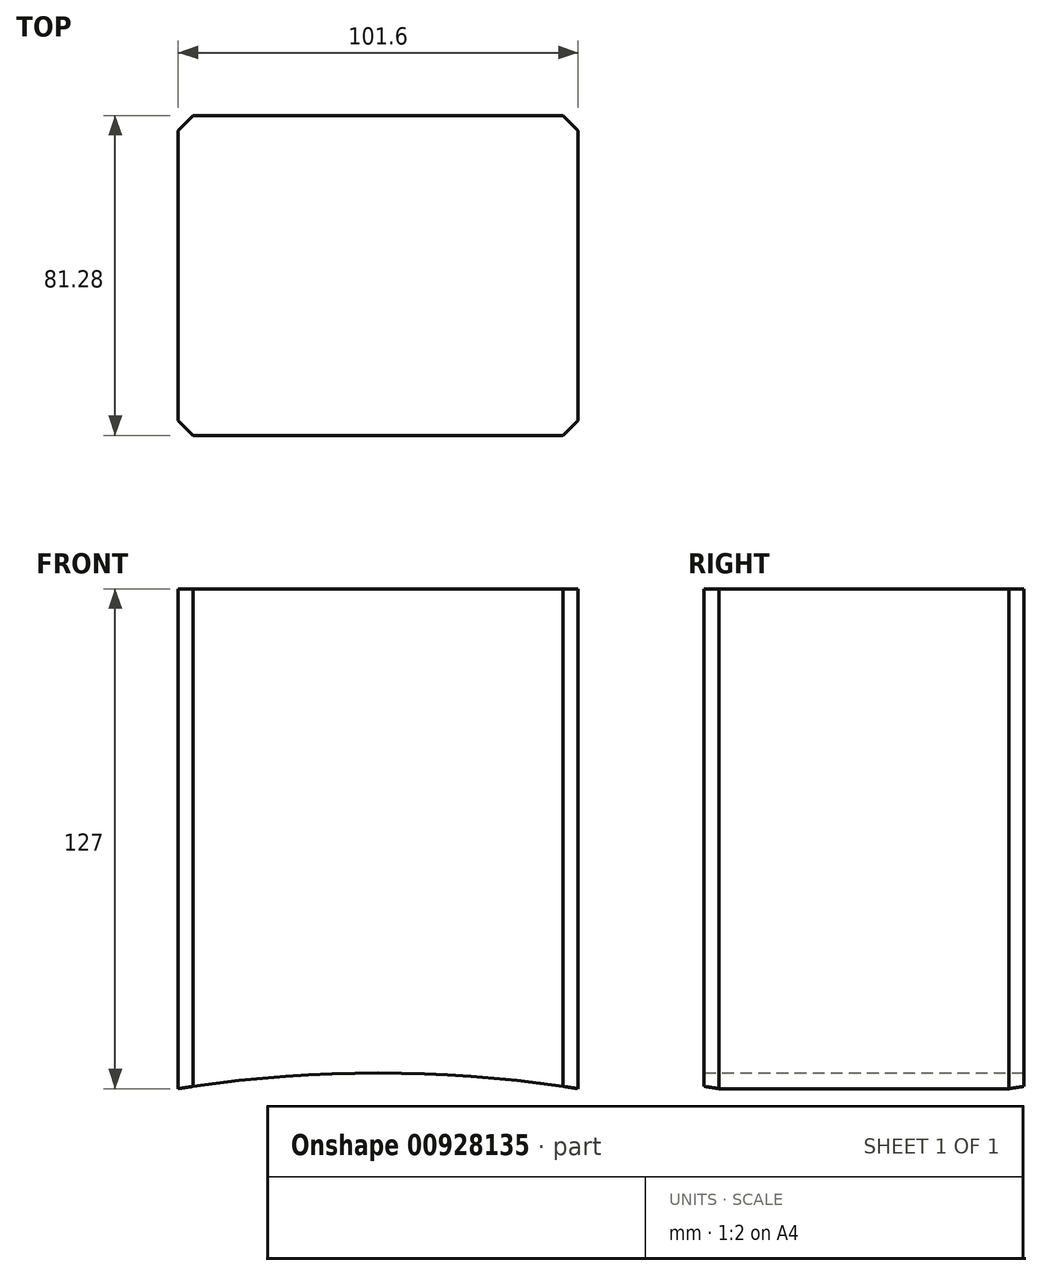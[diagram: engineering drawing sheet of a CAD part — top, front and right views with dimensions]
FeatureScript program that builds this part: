
annotation { "Feature Type Name" : "Feature", "Feature Type Description" : "" }
export const myFeature = defineFeature(function(context is Context, id is Id, definition is map)
    precondition{}
    {
        {
            var Q0;
            Q0=qCreatedBy(makeId("Front.planeOp"),FACE);
            var sketch = newSketch(context, id + "F0", { "sketchPlane" : qUnion([Q0])});
            skArc(sketch, "E0", {"start": v(58.46, 0) * mm, "mid": v(7.66, 4) * mm, "end": v(-43.14, 0) * mm});
            skLineSegment(sketch, "E1", {"start": v(58.46, 0) * mm, "end": v(58.46, 127) * mm});
            skLineSegment(sketch, "E2", {"start": v(58.46, 127) * mm, "end": v(-43.14, 127) * mm});
            skLineSegment(sketch, "E3", {"start": v(-43.14, 127) * mm, "end": v(-43.14, 0) * mm});
            skSolve(sketch);
        }
        {
            var Q0;
            Q0=makeQuery(id+"F0.imprint","IMPRINT",FACE,{"disambiguationData":[TD([[makeQuery(id+"F0.imprint","IMPRINT",EDGE,{"derivedFrom":sQuery(id+"F0.wireOp",EDGE,"E0")}),-1.0]])]});
            extrude(context, id + "F1", {"entities" : qUnion([Q0]), "depth" : 81.28 * mm, "offsetDistance" : 25.4 * mm});
        }
        {
            var Q0;
            Q0=makeQuery(id+"F1.opExtrude","CAP_EDGE",EDGE,{"disambiguationData":[OSD([sQuery(id+"F0.wireOp",EDGE,"E3")])],"isStart":false});
            var Q1;
            Q1=makeQuery(id+"F1.opExtrude","CAP_EDGE",EDGE,{"disambiguationData":[OSD([sQuery(id+"F0.wireOp",EDGE,"E1")])],"isStart":false});
            var Q2;
            Q2=makeQuery(id+"F1.opExtrude","CAP_EDGE",EDGE,{"disambiguationData":[OSD([sQuery(id+"F0.wireOp",EDGE,"E3")])],"isStart":true});
            var Q3;
            Q3=makeQuery(id+"F1.opExtrude","CAP_EDGE",EDGE,{"disambiguationData":[OSD([sQuery(id+"F0.wireOp",EDGE,"E1")])],"isStart":true});
            chamfer(context, id + "F2", {"entities" : qUnion([Q0, Q1, Q2, Q3]), "width" : 3.8 * mm, "tangentPropagation" : true});
        }
    });
